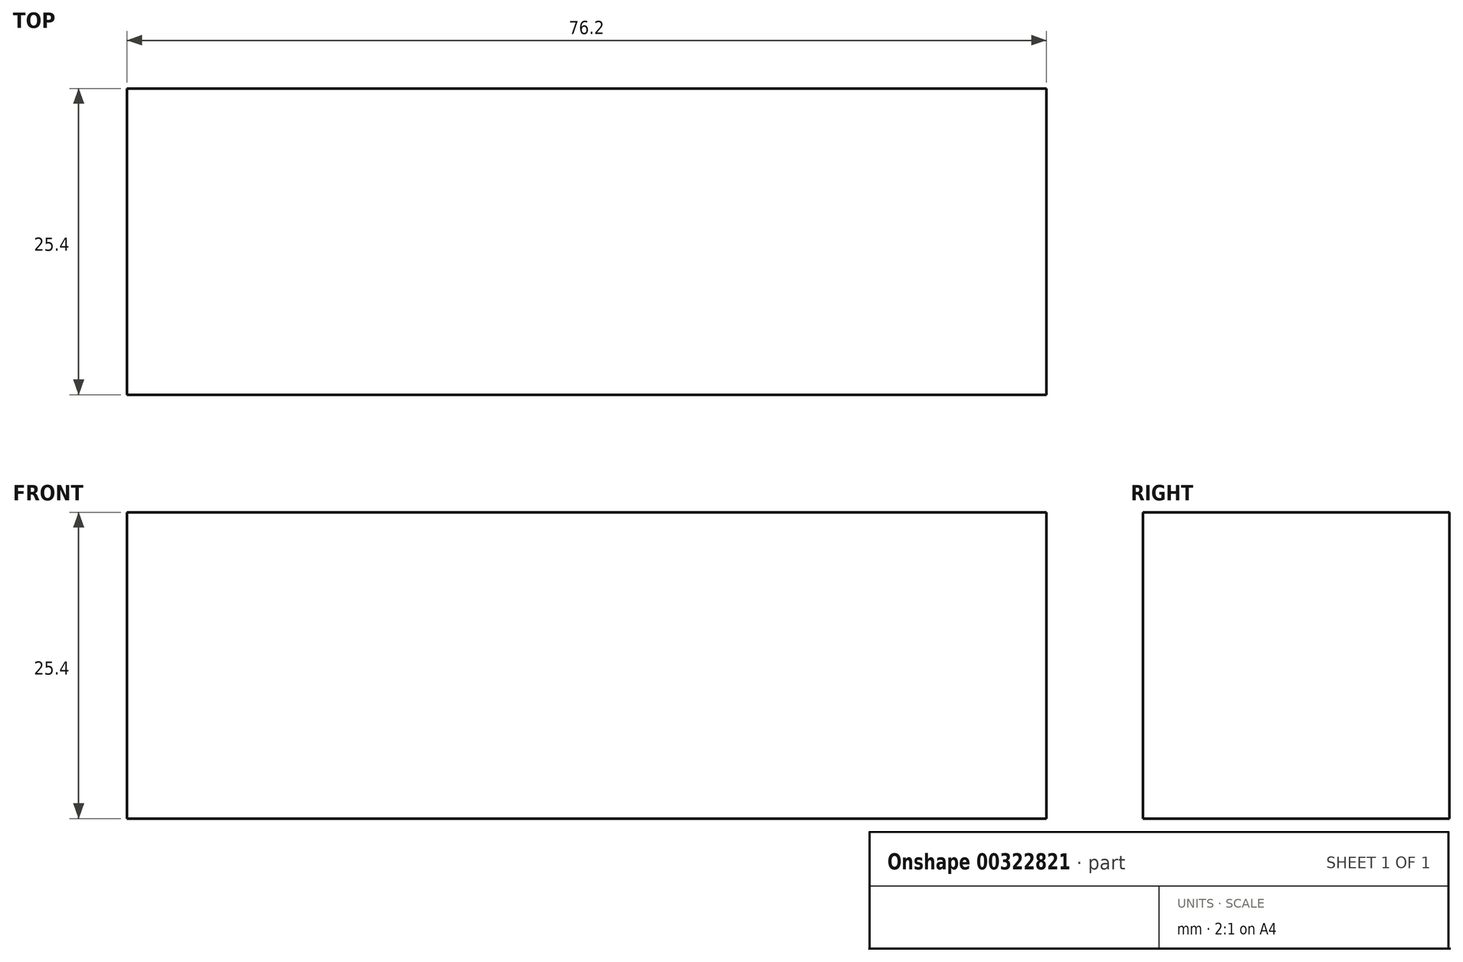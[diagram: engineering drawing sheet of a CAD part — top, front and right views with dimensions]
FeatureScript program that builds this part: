
annotation { "Feature Type Name" : "Feature", "Feature Type Description" : "" }
export const myFeature = defineFeature(function(context is Context, id is Id, definition is map)
    precondition{}
    {
        {
            var Q0;
            Q0=qCreatedBy(makeId("Front.planeOp"),FACE);
            var sketch = newSketch(context, id + "F0", { "sketchPlane" : qUnion([Q0])});
            skLineSegment(sketch, "E0.bottom", {"start": v(-131.45, 37.95) * mm, "end": v(-55.25, 37.95) * mm});
            skLineSegment(sketch, "E0.top", {"start": v(-131.45, 12.55) * mm, "end": v(-55.25, 12.55) * mm});
            skLineSegment(sketch, "E0.left", {"start": v(-131.45, 37.95) * mm, "end": v(-131.45, 12.55) * mm});
            skLineSegment(sketch, "E0.right", {"start": v(-55.25, 37.95) * mm, "end": v(-55.25, 12.55) * mm});
            skSolve(sketch);
        }
        {
            var Q0;
            Q0 = qSketchRegion(id + "F0", true);
            var Q1;
            Q1=sQuery(id+"F0.wireOp",EDGE,"E0.bottom");
            var Q2;
            Q2=sQuery(id+"F0.wireOp",EDGE,"E0.left");
            var Q3;
            Q3=sQuery(id+"F0.wireOp",EDGE,"E0.top");
            var Q4;
            Q4=sQuery(id+"F0.wireOp",EDGE,"E0.right");
            extrude(context, id + "F1", {"entities" : qUnion([Q0]), "bodyType" : ToolBodyType.SURFACE, "surfaceEntities" : qUnion([Q1, Q2, Q3, Q4]), "endBound" : BoundingType.SYMMETRIC, "depth" : 25.4 * mm});
        }
    });
